# Revit family: Shower-Shower_Door-KOHLER-Aerie-K-707105_1
name_source: partatom
category: Specialty Equipment
revit_build: Autodesk Revit 2017 (Build: 20160225_1515(x64)
units: mm (PartAtom-declared; Revit-internal decimal feet)

## family parameters
Cut with Voids When Loaded = No
Host = Face
OmniClass Number = 23.31.17.17
Part Type = Normal
Room Calculation Point = No
Round Connector Dimension = Use Diameter
Shared = No

## types (1)
- SHP-Bright Polished Silver
    ADA Compliant = No
    Assembly Code = C1030200
    Date Modified = 08/20/2020
    Default Elevation = 0"
    Description = Bath screen, 56-15/16 inch H x 32 inch W with 1/4 inch thick Crystal Clear glass and square corner
    Finish = Kohler-Metal-SHP-Bright_Polished_Silver
    Glass Finish = Kohler-Glass-L-Crystal_Clear
    Height = 57"
    Length = 1 1/4"
    Manufacturer = KOHLER Co.
    Master Format 2014 = 10 28 00
    Master Format 2014 Name = Toilet, Bath, and Laundry Accessories
    Material = Premium Metal Construction
    Model = K-707105-L-SHP
    Product Documentation Link = https://www.us.kohler.com
    Product Name = Aerie
    Product Page URL = http://www.us.kohler.com
    Type = 1
    URL = https://www.us.kohler.com
    WaterSense Certified = No

## geometry (parser evidence)
native form markers: Sweep x5
no freeform markers — native parametric forms only
